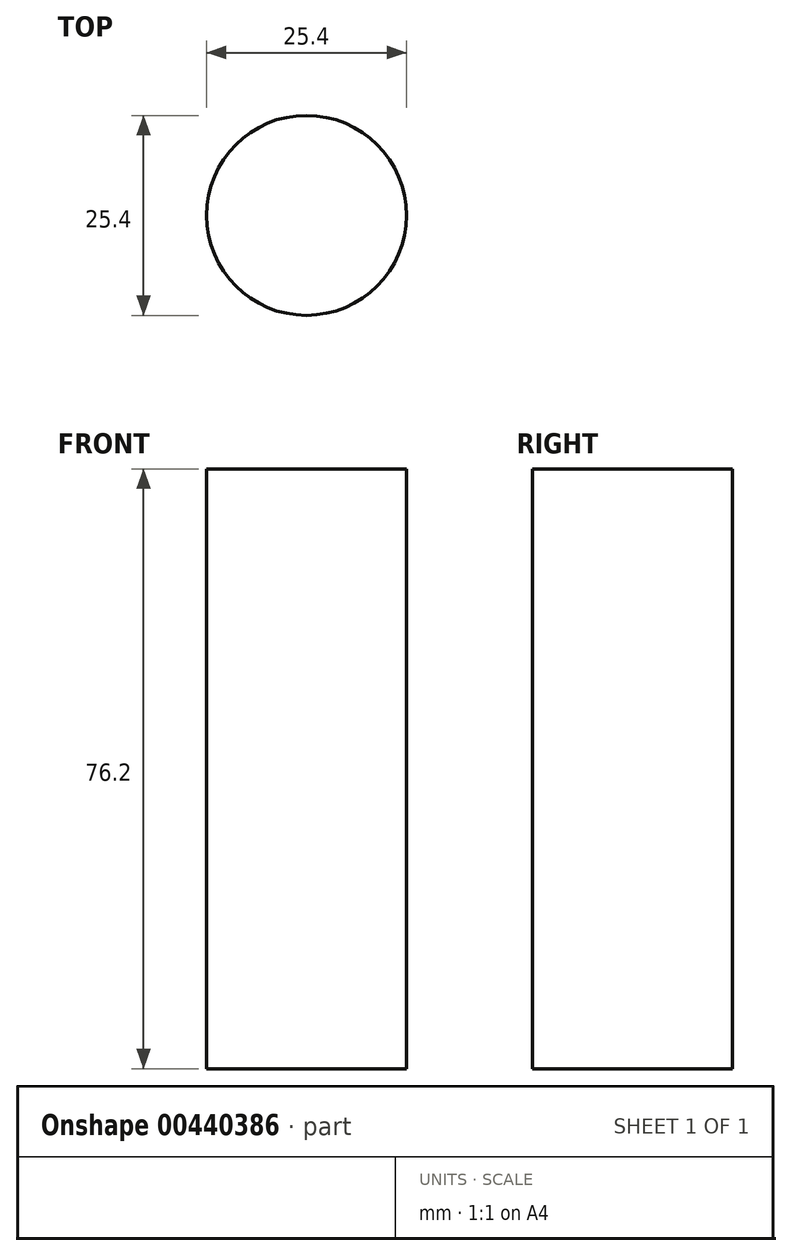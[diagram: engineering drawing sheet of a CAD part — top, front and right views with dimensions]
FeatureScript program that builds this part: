
annotation { "Feature Type Name" : "Feature", "Feature Type Description" : "" }
export const myFeature = defineFeature(function(context is Context, id is Id, definition is map)
    precondition{}
    {
        {
            var Q0;
            Q0=qCreatedBy(makeId("Top.planeOp"),FACE);
            var sketch = newSketch(context, id + "F0", { "sketchPlane" : qUnion([Q0])});
            skCircle(sketch, "E0", {"center": v(-28.83, 8.21) * mm, "radius": 12.7 * mm});
            skSolve(sketch);
        }
        {
            var Q0;
            Q0=makeQuery(id+"F0.imprint","IMPRINT",FACE,{"disambiguationData":[TD([[makeQuery(id+"F0.imprint","IMPRINT",EDGE,{"derivedFrom":sQuery(id+"F0.wireOp",EDGE,"E0")}),1.0]])]});
            extrude(context, id + "F1", {"entities" : qUnion([Q0]), "depth" : 76.2 * mm});
        }
    });
